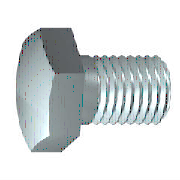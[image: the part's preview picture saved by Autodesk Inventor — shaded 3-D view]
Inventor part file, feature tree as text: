
AUTODESK INVENTOR PART (.ipt)
format: ipt  version: 2025.1 (Build 291241020, 241B)  size: 211,968 bytes
history: native  units: mm (DEFAULTED — no unit token found)
features: other x3, revolve x2, extrude x2, sketch x2, fillet x1
ambient origin geometry x8: Origin, YZ Plane, XZ Plane, XY Plane, X Axis, Y Axis, Z Axis, Center Point
bodies: Solid1 (feature_tree)
feature tree (10):
  revolve  "Revolution1"  Angle=45.0deg
  extrude  "Extrusion1"  TaperAngle=60.0deg  [1 undecoded]
  revolve  "Revolution2"  [1 undecoded]
  extrude  "Extrusion2"  TaperAngle=30.0deg  [1 undecoded]
  other  "MSC_A1"
  other  "MSC_PF1"
  other  "MSC_PT1"
  fillet  "Fillet1"  [1 undecoded]
  sketch  "Sketch2"  dims[d3=30.0deg d5=45.0deg]
  sketch  "Sketch4"  dims[d8=90.0deg d9=60.0deg d13=0.0mm d14=30.0deg d16=90.0deg d18=0.0mm d22=0.0mm d23=0.0mm d25=0.0mm d26=0.0mm d27=13.5mm d28=1.5mm d29=0.0mm d30=0.6mm d31=0.0mm]
note: 4 required parameter values undecoded (feature->parameter linkage not recoverable at this tier; creation-order binding heuristic only, values carry confidence <= 0.55)